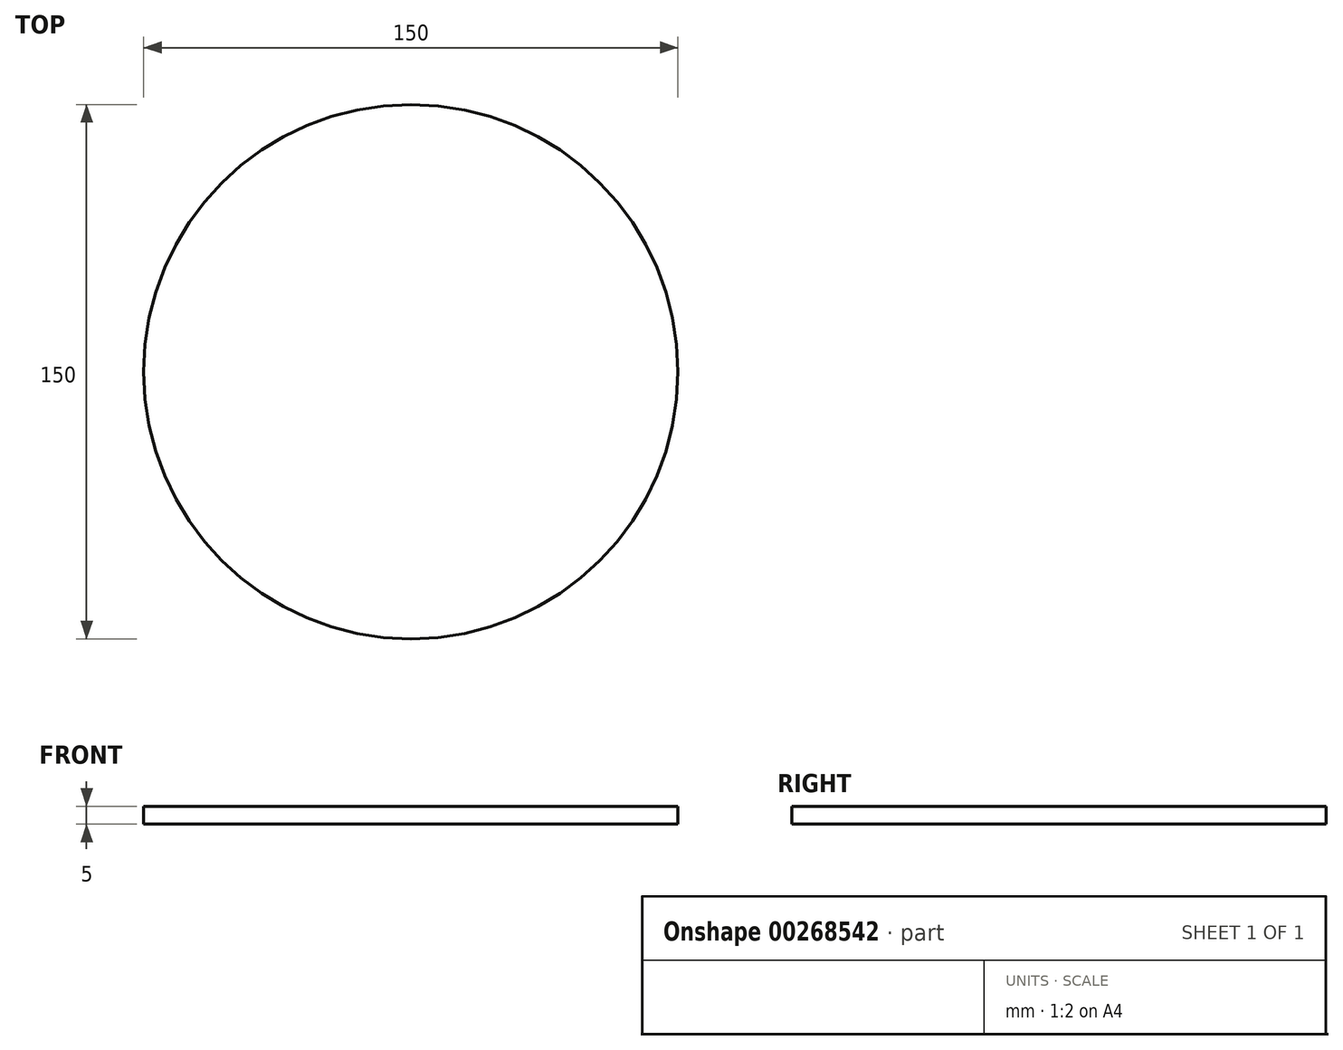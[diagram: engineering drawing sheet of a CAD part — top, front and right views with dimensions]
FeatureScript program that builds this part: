
annotation { "Feature Type Name" : "Feature", "Feature Type Description" : "" }
export const myFeature = defineFeature(function(context is Context, id is Id, definition is map)
    precondition{}
    {
        {
            var Q0;
            Q0=qCreatedBy(makeId("Top.planeOp"),FACE);
            var sketch = newSketch(context, id + "F0", { "sketchPlane" : qUnion([Q0])});
            skCircle(sketch, "E0", {"center": v(0, 0) * mm, "radius": 75 * mm});
            skSolve(sketch);
        }
        {
            var Q0;
            Q0=makeQuery(id+"F0.imprint","IMPRINT",FACE,{"disambiguationData":[TD([[makeQuery(id+"F0.imprint","IMPRINT",EDGE,{"derivedFrom":sQuery(id+"F0.wireOp",EDGE,"E0")}),1.0]])]});
            extrude(context, id + "F1", {"entities" : qUnion([Q0]), "depth" : 5 * mm});
        }
    });
